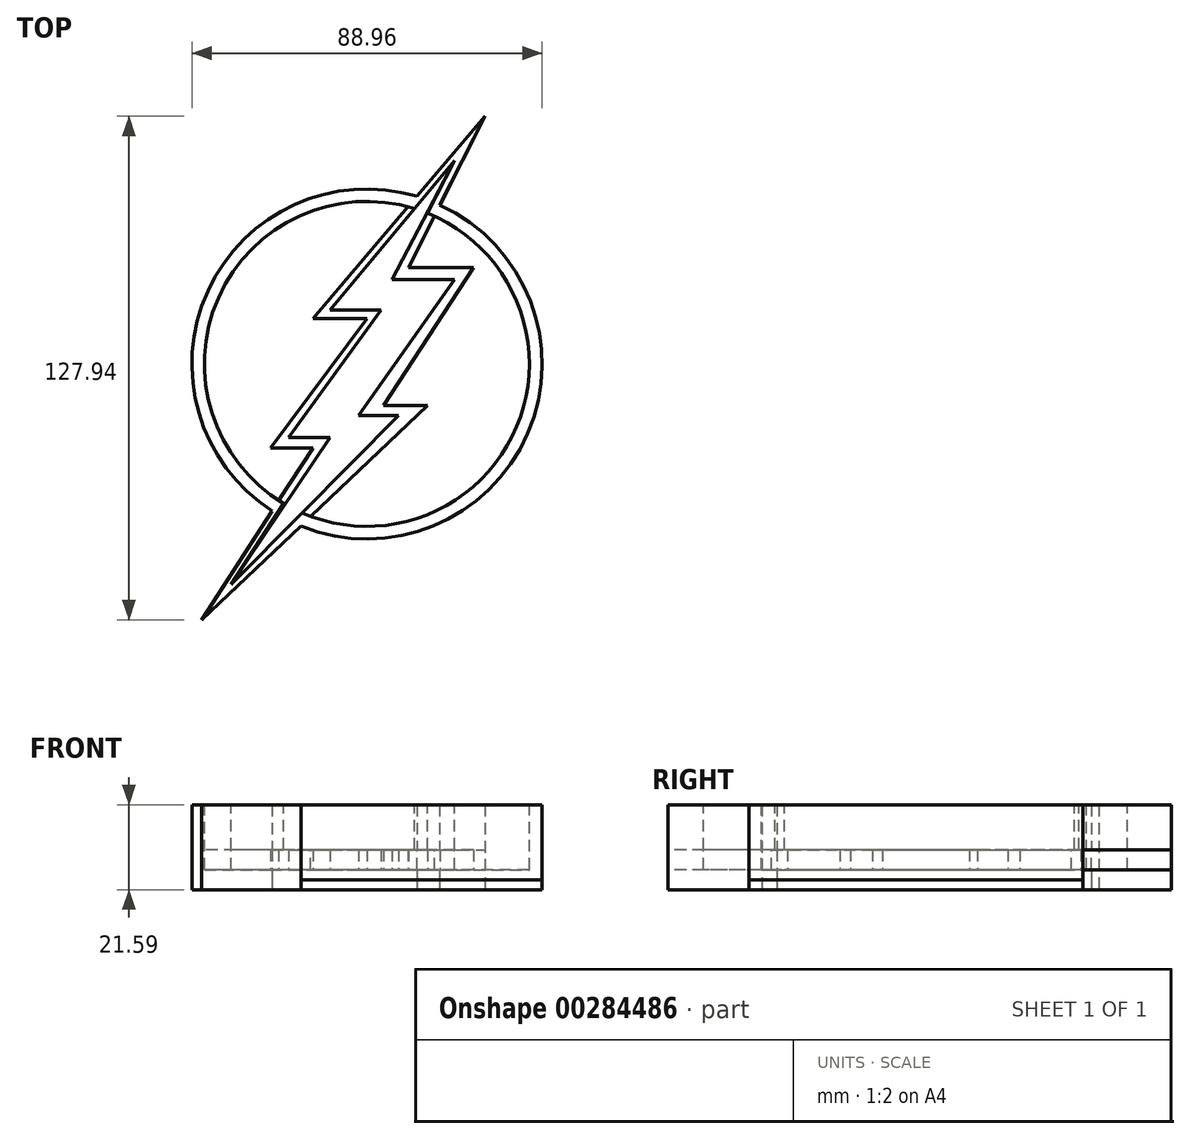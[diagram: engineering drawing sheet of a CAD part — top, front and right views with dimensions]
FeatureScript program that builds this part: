
annotation { "Feature Type Name" : "Feature", "Feature Type Description" : "" }
export const myFeature = defineFeature(function(context is Context, id is Id, definition is map)
    precondition{}
    {
        {
            var Q0;
            Q0=qCreatedBy(makeId("Top.planeOp"),FACE);
            var sketch = newSketch(context, id + "F0", { "sketchPlane" : qUnion([Q0])});
            skCircle(sketch, "E0", {"center": v(0, 0) * mm, "radius": 44.45 * mm});
            skLineSegment(sketch, "E1", {"start": v(29.99, 62.94) * mm, "end": v(-13.69, 11.56) * mm});
            skLineSegment(sketch, "E2", {"start": v(-13.69, 11.56) * mm, "end": v(0, 11.56) * mm});
            skLineSegment(sketch, "E3", {"start": v(0, 11.56) * mm, "end": v(-24.48, -21.32) * mm});
            skLineSegment(sketch, "E4", {"start": v(-24.48, -21.32) * mm, "end": v(-13.69, -21.32) * mm});
            skLineSegment(sketch, "E5", {"start": v(-13.69, -21.32) * mm, "end": v(-41.95, -65) * mm});
            skLineSegment(sketch, "E6", {"start": v(-41.95, -65) * mm, "end": v(15.6, -10.53) * mm});
            skLineSegment(sketch, "E7", {"start": v(15.6, -10.53) * mm, "end": v(4.3, -10.53) * mm});
            skLineSegment(sketch, "E8", {"start": v(4.3, -10.53) * mm, "end": v(26.99, 24.53) * mm});
            skLineSegment(sketch, "E9", {"start": v(26.99, 24.53) * mm, "end": v(10.46, 24.53) * mm});
            skLineSegment(sketch, "E10", {"start": v(10.46, 24.53) * mm, "end": v(29.99, 62.94) * mm});
            skSolve(sketch);
        }
        {
            var Q0;
            Q0 = qSketchRegion(id + "F0", true);
            extrude(context, id + "F1", {"entities" : qUnion([Q0]), "depth" : 2.54 * mm});
        }
        {
            var Q0;
            Q0=makeQuery(id+"F1.opExtrude","CAP_FACE",FACE,{"disambiguationData":[OSD([sQuery(id+"F0.wireOp",EDGE,"E0"),sQuery(id+"F0.wireOp",EDGE,"E1"),sQuery(id+"F0.wireOp",EDGE,"E5"),sQuery(id+"F0.wireOp",EDGE,"E6"),sQuery(id+"F0.wireOp",EDGE,"E10")])],"isStart":false});
            var sketch = newSketch(context, id + "F2", { "sketchPlane" : qUnion([Q0])});
            skLineSegment(sketch, "E11", {"start": v(29.99, 62.94) * mm, "end": v(12.7, 42.6) * mm});
            skArc(sketch, "E12", {"start": v(12.7, 42.6) * mm, "mid": v(-40.4, 18.57) * mm, "end": v(-24.07, -37.37) * mm});
            skLineSegment(sketch, "E13", {"start": v(-24.07, -37.37) * mm, "end": v(-41.95, -65) * mm});
            skLineSegment(sketch, "E14", {"start": v(-41.95, -65) * mm, "end": v(-16.77, -41.17) * mm});
            skArc(sketch, "E15", {"start": v(-16.77, -41.17) * mm, "mid": v(40.85, -17.68) * mm, "end": v(18.53, 40.4) * mm});
            skLineSegment(sketch, "E16", {"start": v(18.53, 40.4) * mm, "end": v(29.99, 62.94) * mm});
            skSolve(sketch);
        }
        {
            var Q0;
            Q0 = qSketchRegion(id + "F2", true);
            extrude(context, id + "F3", {"entities" : qUnion([Q0]), "operationType" : NewBodyOperationType.ADD, "depth" : 19.05 * mm});
        }
        {
            var Q0;
            Q0=makeQuery(id+"F3.opExtrude","CAP_FACE",FACE,{"disambiguationData":[OSD([sQuery(id+"F2.wireOp",EDGE,"E11"),sQuery(id+"F2.wireOp",EDGE,"E12"),sQuery(id+"F2.wireOp",EDGE,"E13"),sQuery(id+"F2.wireOp",EDGE,"E14"),sQuery(id+"F2.wireOp",EDGE,"E15"),sQuery(id+"F2.wireOp",EDGE,"E16")])],"isStart":false});
            var sketch = newSketch(context, id + "F4", { "sketchPlane" : qUnion([Q0])});
            skCircle(sketch, "E17", {"center": v(0, 0) * mm, "radius": 41.28 * mm});
            skSolve(sketch);
        }
        {
            var Q0;
            Q0 = qSketchRegion(id + "F4", true);
            extrude(context, id + "F5", {"entities" : qUnion([Q0]), "operationType" : NewBodyOperationType.REMOVE, "oppositeDirection" : true, "depth" : 16.5 * mm});
        }
        {
            var Q0;
            Q0=makeQuery(id+"F3.opExtrude","CAP_FACE",FACE,{"disambiguationData":[OSD([sQuery(id+"F2.wireOp",EDGE,"E11"),sQuery(id+"F2.wireOp",EDGE,"E12"),sQuery(id+"F2.wireOp",EDGE,"E13"),sQuery(id+"F2.wireOp",EDGE,"E14"),sQuery(id+"F2.wireOp",EDGE,"E15"),sQuery(id+"F2.wireOp",EDGE,"E16")])],"isStart":false});
            var sketch = newSketch(context, id + "F6", { "sketchPlane" : qUnion([Q0])});
            skLineSegment(sketch, "E18", {"start": v(22.27, 51.67) * mm, "end": v(12.12, 39.46) * mm});
            skPoint(sketch, "E18.startSnap0", {"position": v(24.26, 51.67) * mm});
            skLineSegment(sketch, "E19", {"start": v(12.12, 39.46) * mm, "end": v(22.27, 51.67) * mm});
            skLineSegment(sketch, "E20", {"start": v(22.27, 51.67) * mm, "end": v(15.46, 38.27) * mm});
            skLineSegment(sketch, "E21", {"start": v(15.46, 38.27) * mm, "end": v(12.12, 39.46) * mm});
            skSolve(sketch);
        }
        {
            var Q0;
            Q0 = qSketchRegion(id + "F6", true);
            extrude(context, id + "F7", {"entities" : qUnion([Q0]), "operationType" : NewBodyOperationType.REMOVE, "oppositeDirection" : true, "depth" : 16.5 * mm});
        }
        {
            var Q0;
            Q0=makeQuery(id+"F3.opExtrude","CAP_FACE",FACE,{"disambiguationData":[OSD([sQuery(id+"F2.wireOp",EDGE,"E11"),sQuery(id+"F2.wireOp",EDGE,"E12"),sQuery(id+"F2.wireOp",EDGE,"E13"),sQuery(id+"F2.wireOp",EDGE,"E14"),sQuery(id+"F2.wireOp",EDGE,"E15"),sQuery(id+"F2.wireOp",EDGE,"E16")])],"isStart":false});
            var sketch = newSketch(context, id + "F8", { "sketchPlane" : qUnion([Q0])});
            skLineSegment(sketch, "E22", {"start": v(-34.49, -56.03) * mm, "end": v(-21.16, -35.44) * mm});
            skLineSegment(sketch, "E23", {"start": v(-21.16, -35.44) * mm, "end": v(-16.48, -37.84) * mm});
            skLineSegment(sketch, "E24", {"start": v(-16.48, -37.84) * mm, "end": v(-34.49, -56.03) * mm});
            skSolve(sketch);
        }
        {
            var Q0;
            Q0 = qSketchRegion(id + "F8", true);
            extrude(context, id + "F9", {"entities" : qUnion([Q0]), "operationType" : NewBodyOperationType.REMOVE, "oppositeDirection" : true, "depth" : 16.5 * mm});
        }
        {
            var Q0;
            Q0=makeQuery(id+"F9.boolean.opBoolean","MERGE",FACE,{"derivedFrom":[makeQuery(id+"F7.boolean.opBoolean","MERGE",FACE,{"derivedFrom":[makeQuery(id+"F5.boolean.opBoolean","COPY",FACE,{"derivedFrom":makeQuery(id+"F5.opExtrude","CAP_FACE",FACE,{"disambiguationData":[OSD([sQuery(id+"F4.wireOp",EDGE,"E17")])],"isStart":false})}),makeQuery(id+"F7.opExtrude","CAP_FACE",FACE,{"disambiguationData":[OSD([sQuery(id+"F6.wireOp",EDGE,"E19"),sQuery(id+"F6.wireOp",EDGE,"E20"),sQuery(id+"F6.wireOp",EDGE,"E21")])],"isStart":false})]}),makeQuery(id+"F9.opExtrude","CAP_FACE",FACE,{"disambiguationData":[OSD([sQuery(id+"F8.wireOp",EDGE,"E22"),sQuery(id+"F8.wireOp",EDGE,"E23"),sQuery(id+"F8.wireOp",EDGE,"E24")])],"isStart":false})]});
            var sketch = newSketch(context, id + "F10", { "sketchPlane" : qUnion([Q0])});
            skLineSegment(sketch, "E25", {"start": v(22.27, 51.67) * mm, "end": v(-9.33, 13.65) * mm});
            skLineSegment(sketch, "E26", {"start": v(-9.33, 13.65) * mm, "end": v(3.66, 13.65) * mm});
            skLineSegment(sketch, "E27", {"start": v(3.66, 13.65) * mm, "end": v(-19.92, -18.66) * mm});
            skLineSegment(sketch, "E28", {"start": v(-19.92, -18.66) * mm, "end": v(-9.33, -18.66) * mm});
            skLineSegment(sketch, "E29", {"start": v(-9.33, -18.66) * mm, "end": v(-34.49, -56.03) * mm});
            skLineSegment(sketch, "E30", {"start": v(-34.49, -56.03) * mm, "end": v(8.06, -13.07) * mm});
            skLineSegment(sketch, "E31", {"start": v(8.06, -13.07) * mm, "end": v(-2.07, -13.07) * mm});
            skLineSegment(sketch, "E32", {"start": v(-2.07, -13.07) * mm, "end": v(22.27, 21.42) * mm});
            skLineSegment(sketch, "E33", {"start": v(22.27, 21.42) * mm, "end": v(6.47, 21.42) * mm});
            skLineSegment(sketch, "E34", {"start": v(6.47, 21.42) * mm, "end": v(22.27, 51.67) * mm});
            skLineSegment(sketch, "E35", {"start": v(10.44, 39.93) * mm, "end": v(-13.68, 11.57) * mm});
            skLineSegment(sketch, "E36", {"start": v(-13.68, 11.57) * mm, "end": v(0, 11.57) * mm});
            skLineSegment(sketch, "E37", {"start": v(0, 11.57) * mm, "end": v(-24.5, -21.35) * mm});
            skLineSegment(sketch, "E38", {"start": v(-24.5, -21.35) * mm, "end": v(-13.68, -21.35) * mm});
            skLineSegment(sketch, "E39", {"start": v(-13.68, -21.35) * mm, "end": v(-22.36, -34.7) * mm});
            skLineSegment(sketch, "E40", {"start": v(-22.36, -34.7) * mm, "end": v(-41.9, -64.9) * mm});
            skLineSegment(sketch, "E41", {"start": v(-41.9, -64.9) * mm, "end": v(15.46, -10.56) * mm});
            skLineSegment(sketch, "E42", {"start": v(15.46, -10.56) * mm, "end": v(4.3, -10.56) * mm});
            skLineSegment(sketch, "E43", {"start": v(4.3, -10.56) * mm, "end": v(27.09, 24.44) * mm});
            skLineSegment(sketch, "E44", {"start": v(27.09, 24.44) * mm, "end": v(10.57, 24.44) * mm});
            skLineSegment(sketch, "E45", {"start": v(10.57, 24.44) * mm, "end": v(29.98, 62.93) * mm});
            skLineSegment(sketch, "E46", {"start": v(29.98, 62.93) * mm, "end": v(10.44, 39.93) * mm});
            skSolve(sketch);
        }
        {
            var Q0;
            Q0 = qSketchRegion(id + "F10", true);
            extrude(context, id + "F11", {"entities" : qUnion([Q0]), "operationType" : NewBodyOperationType.ADD, "depth" : 5.08 * mm});
        }
    });
